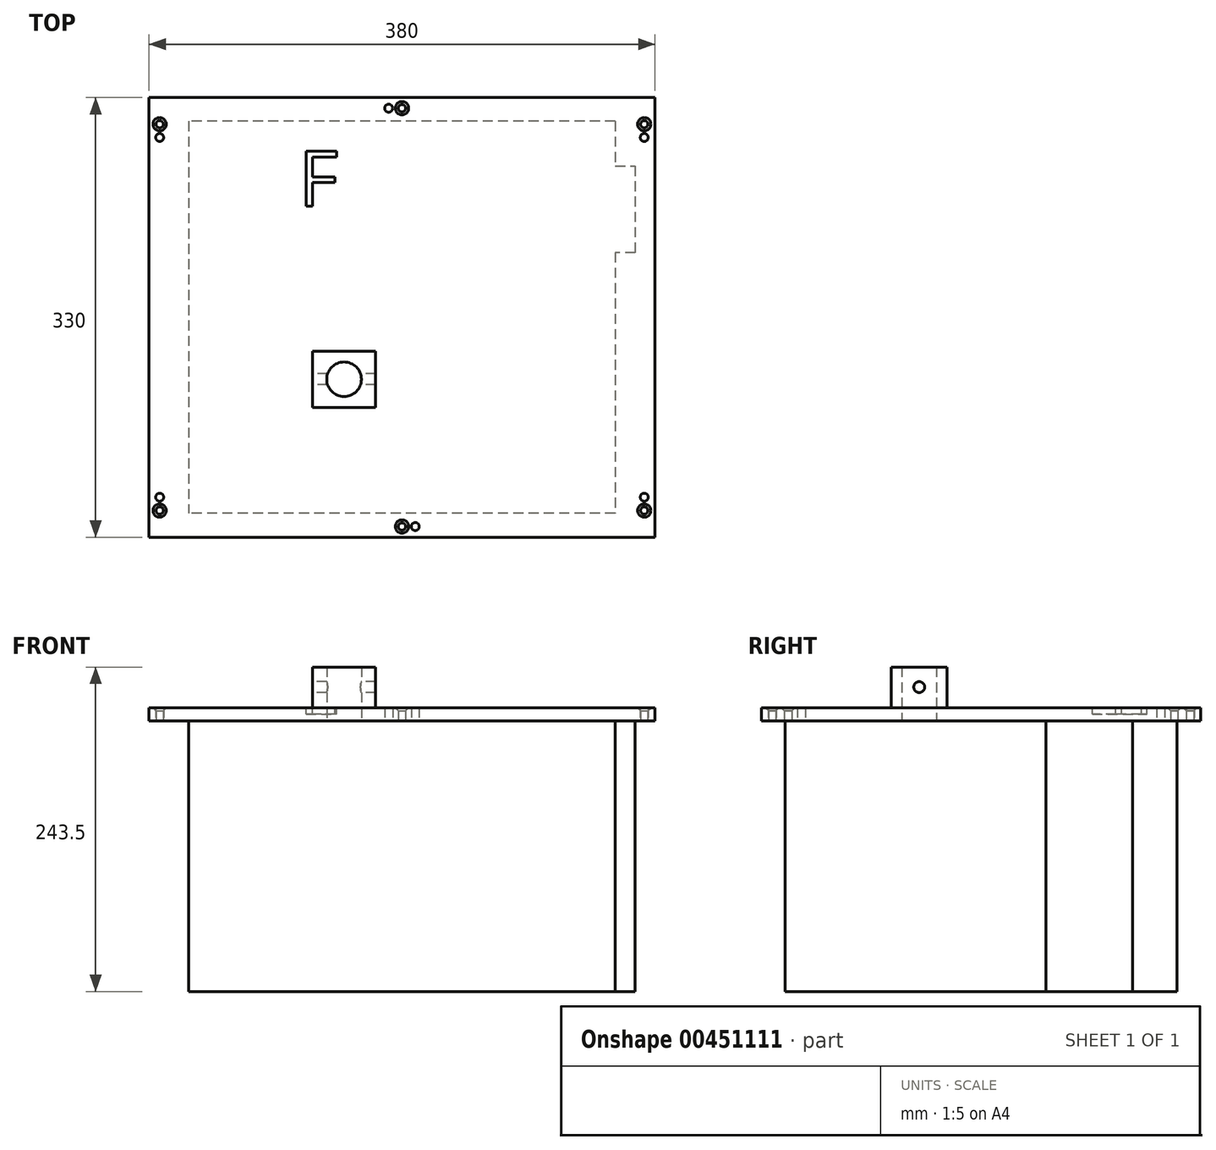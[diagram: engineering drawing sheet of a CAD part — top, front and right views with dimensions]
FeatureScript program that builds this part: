
annotation { "Feature Type Name" : "Feature", "Feature Type Description" : "" }
export const myFeature = defineFeature(function(context is Context, id is Id, definition is map)
    precondition{}
    {
        {
            var Q0;
            Q0=qCreatedBy(makeId("Top.planeOp"),FACE);
            var sketch = newSketch(context, id + "F0", { "sketchPlane" : qUnion([Q0])});
            skLineSegment(sketch, "E0.bottom", {"start": v(190, -165) * mm, "end": v(-190, -165) * mm});
            skLineSegment(sketch, "E0.top", {"start": v(190, 165) * mm, "end": v(-190, 165) * mm});
            skLineSegment(sketch, "E0.left", {"start": v(190, -165) * mm, "end": v(190, 165) * mm});
            skLineSegment(sketch, "E0.right", {"start": v(-190, -165) * mm, "end": v(-190, 165) * mm});
            skPoint(sketch, "E0.middle", {"position": v(0, 0) * mm});
            skSolve(sketch);
        }
        {
            var Q0;
            Q0 = qSketchRegion(id + "F0", true);
            extrude(context, id + "F1", {"entities" : qUnion([Q0]), "depth" : 10 * mm});
        }
        {
            var Q0;
            Q0=makeQuery(id+"F1.opExtrude","CAP_FACE",FACE,{"disambiguationData":[OSD([sQuery(id+"F0.wireOp",EDGE,"E0.bottom"),sQuery(id+"F0.wireOp",EDGE,"E0.top"),sQuery(id+"F0.wireOp",EDGE,"E0.left"),sQuery(id+"F0.wireOp",EDGE,"E0.right")])],"isStart":true});
            var sketch = newSketch(context, id + "F2", { "sketchPlane" : qUnion([Q0])});
            skLineSegment(sketch, "E1.bottom", {"start": v(160.15, -147.15) * mm, "end": v(-160.15, -147.15) * mm});
            skLineSegment(sketch, "E1.top", {"start": v(160.15, 147.15) * mm, "end": v(-160.15, 147.15) * mm});
            skLineSegment(sketch, "E1.left", {"start": v(160.15, -147.15) * mm, "end": v(160.15, 147.15) * mm});
            skLineSegment(sketch, "E1.right", {"start": v(-160.15, -147.15) * mm, "end": v(-160.15, 147.15) * mm});
            skPoint(sketch, "E1.middle", {"position": v(0, 0) * mm});
            skLineSegment(sketch, "E2", {"start": v(160.15, -113.65) * mm, "end": v(175.15, -113.65) * mm});
            skLineSegment(sketch, "E3", {"start": v(175.15, -113.65) * mm, "end": v(175.15, -48.65) * mm});
            skLineSegment(sketch, "E4", {"start": v(175.15, -48.65) * mm, "end": v(160.15, -48.65) * mm});
            skSolve(sketch);
        }
        {
            var Q0;
            Q0 = qSketchRegion(id + "F2", true);
            extrude(context, id + "F3", {"entities" : qUnion([Q0]), "operationType" : NewBodyOperationType.ADD, "depth" : 203 * mm});
        }
        {
            var Q0;
            {var subQ0=sQuery(id+"F0.wireOp",EDGE,"E0.left");var subQ1=sQuery(id+"F0.wireOp",EDGE,"E0.top");var subQ2=sQuery(id+"F0.wireOp",EDGE,"E0.right");var subQ3=sQuery(id+"F0.wireOp",EDGE,"E0.bottom");Q0=makeQuery(id+"F8.boolean.opBoolean","SPLIT",FACE,{"disambiguationData":[TD([makeQuery(id+"F1.opExtrude","SWEPT_FACE",FACE,{"disambiguationData":[OSD([subQ3])]})])],"derivedFrom":makeQuery(id+"F1.opExtrude","CAP_FACE",FACE,{"disambiguationData":[OSD([subQ3,subQ1,subQ0,subQ2])],"isStart":false})});}
            var sketch = newSketch(context, id + "F4", { "sketchPlane" : qUnion([Q0])});
            skPoint(sketch, "E5", {"position": v(0, 157) * mm});
            skPoint(sketch, "E6", {"position": v(0, -157) * mm});
            skPoint(sketch, "E7", {"position": v(-182, 145) * mm});
            skPoint(sketch, "E8", {"position": v(-182, -145) * mm});
            skPoint(sketch, "E9", {"position": v(-182, 135) * mm});
            skPoint(sketch, "E10", {"position": v(-182, -135) * mm});
            skPoint(sketch, "E11.MirrorP", {"position": v(182, 145) * mm});
            skPoint(sketch, "E12.MirrorP", {"position": v(182, -145) * mm});
            skPoint(sketch, "E13.MirrorP", {"position": v(182, 135) * mm});
            skPoint(sketch, "E14.MirrorP", {"position": v(182, -135) * mm});
            skPoint(sketch, "E15", {"position": v(-10, 157) * mm});
            skPoint(sketch, "E16", {"position": v(10, -157) * mm});
            skPoint(sketch, "E17.middle", {"position": v(0, 0) * mm});
            skPoint(sketch, "E18", {"position": v(-43.5, -46.5) * mm});
            skSolve(sketch);
        }
        {
            var Q0;
            Q0=sQuery(id+"F4.wireOp",VERTEX,"E9");
            var Q1;
            Q1=sQuery(id+"F4.wireOp",VERTEX,"E10");
            var Q2;
            Q2=sQuery(id+"F4.wireOp",VERTEX,"E13.MirrorP");
            var Q3;
            Q3=sQuery(id+"F4.wireOp",VERTEX,"E14.MirrorP");
            var Q4;
            Q4=sQuery(id+"F4.wireOp",VERTEX,"E16");
            var Q5;
            Q5=sQuery(id+"F4.wireOp",VERTEX,"E15");
            var Q6;
            Q6=makeQuery(id+"F1.opExtrude","SWEPT_BODY",BODY,{"disambiguationData":[OSD([sQuery(id+"F0.wireOp",EDGE,"E0.bottom"),sQuery(id+"F0.wireOp",EDGE,"E0.top"),sQuery(id+"F0.wireOp",EDGE,"E0.left"),sQuery(id+"F0.wireOp",EDGE,"E0.right")])]});
            hole(context, id + "F5", {"style" : HoleStyle.SIMPLE, "endStyle" : HoleEndStyle.BLIND, "holeDiameter" : 6 * mm, "holeDepth" : 10 * mm, "tappedDepth" : 12 * mm, "tapClearance" : 3, "locations" : qUnion([Q0, Q1, Q2, Q3, Q4, Q5]), "scope" : qUnion([Q6])});
        }
        {
            var Q0;
            Q0=sQuery(id+"F4.wireOp",VERTEX,"E7");
            var Q1;
            Q1=sQuery(id+"F4.wireOp",VERTEX,"E11.MirrorP");
            var Q2;
            Q2=sQuery(id+"F4.wireOp",VERTEX,"E8");
            var Q3;
            Q3=sQuery(id+"F4.wireOp",VERTEX,"E12.MirrorP");
            var Q4;
            Q4=sQuery(id+"F4.wireOp",VERTEX,"E6");
            var Q5;
            Q5=sQuery(id+"F4.wireOp",VERTEX,"E5");
            var Q6;
            Q6=makeQuery(id+"F1.opExtrude","SWEPT_BODY",BODY,{"disambiguationData":[OSD([sQuery(id+"F0.wireOp",EDGE,"E0.bottom"),sQuery(id+"F0.wireOp",EDGE,"E0.top"),sQuery(id+"F0.wireOp",EDGE,"E0.left"),sQuery(id+"F0.wireOp",EDGE,"E0.right")])]});
            hole(context, id + "F6", {"style" : HoleStyle.C_SINK, "endStyle" : HoleEndStyle.BLIND, "holeDiameter" : 5.5 * mm, "cSinkDiameter" : 10 * mm, "cSinkAngle" : 90 * degree, "holeDepth" : 10 * mm, "tappedDepth" : 12 * mm, "tapClearance" : 3, "locations" : qUnion([Q0, Q1, Q2, Q3, Q4, Q5]), "scope" : qUnion([Q6])});
        }
        {
            var Q0;
            Q0=makeQuery(id+"F1.opExtrude","CAP_FACE",FACE,{"disambiguationData":[OSD([sQuery(id+"F0.wireOp",EDGE,"E0.bottom"),sQuery(id+"F0.wireOp",EDGE,"E0.top"),sQuery(id+"F0.wireOp",EDGE,"E0.left"),sQuery(id+"F0.wireOp",EDGE,"E0.right")])],"isStart":false});
            var sketch = newSketch(context, id + "F7", { "sketchPlane" : qUnion([Q0])});
            skLineSegment(sketch, "E19.bottom", {"start": v(-19.75, -67.5) * mm, "end": v(-67.25, -67.5) * mm});
            skLineSegment(sketch, "E19.top", {"start": v(-19.75, -25.5) * mm, "end": v(-67.25, -25.5) * mm});
            skLineSegment(sketch, "E19.left", {"start": v(-19.75, -67.5) * mm, "end": v(-19.75, -25.5) * mm});
            skLineSegment(sketch, "E19.right", {"start": v(-67.25, -67.5) * mm, "end": v(-67.25, -25.5) * mm});
            skPoint(sketch, "E19.middle", {"position": v(-43.5, -46.5) * mm});
            skCircle(sketch, "E20", {"center": v(-43.5, -46.5) * mm, "radius": 13 * mm});
            skSolve(sketch);
        }
        {
            var Q0;
            Q0 = qSketchRegion(id + "F7", true);
            extrude(context, id + "F8", {"entities" : qUnion([Q0]), "operationType" : NewBodyOperationType.ADD, "depth" : 30.5 * mm});
        }
        {
            var Q0;
            {var subQ0=sQuery(id+"F0.wireOp",EDGE,"E0.left");var subQ1=sQuery(id+"F0.wireOp",EDGE,"E0.top");var subQ2=sQuery(id+"F0.wireOp",EDGE,"E0.right");var subQ3=sQuery(id+"F0.wireOp",EDGE,"E0.bottom");Q0=makeQuery(id+"F8.boolean.opBoolean","SPLIT",FACE,{"disambiguationData":[TD([makeQuery(id+"F1.opExtrude","SWEPT_FACE",FACE,{"disambiguationData":[OSD([subQ3])]})])],"derivedFrom":makeQuery(id+"F1.opExtrude","CAP_FACE",FACE,{"disambiguationData":[OSD([subQ3,subQ1,subQ0,subQ2])],"isStart":false})});}
            var sketch = newSketch(context, id + "F9", { "sketchPlane" : qUnion([Q0])});
            skText(sketch, "E21", { "text": "F", "fontName": "OpenSans-Regular.ttf"});
            const initialGuessF9  = {"E21": [-0.07771, 0.0835, 1, 0, 0.04155]};
            skSetInitialGuess(sketch, initialGuessF9);
            skSolve(sketch);
        }
        {
            var Q0;
            Q0 = qSketchRegion(id + "F9", true);
            extrude(context, id + "F10", {"entities" : qUnion([Q0]), "operationType" : NewBodyOperationType.REMOVE, "oppositeDirection" : true, "depth" : 5 * mm, "offsetDistance" : 25 * mm});
        }
        {
            var Q0;
            Q0=makeQuery(id+"F8.opExtrude","SWEPT_FACE",FACE,{"disambiguationData":[OSD([sQuery(id+"F7.wireOp",EDGE,"E19.right")])]});
            var sketch = newSketch(context, id + "F11", { "sketchPlane" : qUnion([Q0])});
            skCircle(sketch, "E22", {"center": v(46.5, 25.5) * mm, "radius": 4.1 * mm});
            skSolve(sketch);
        }
        {
            var Q0;
            Q0 = qSketchRegion(id + "F11", true);
            extrude(context, id + "F12", {"entities" : qUnion([Q0]), "operationType" : NewBodyOperationType.REMOVE, "oppositeDirection" : true, "depth" : 62.5 * mm, "offsetDistance" : 25 * mm});
        }
        {
            var Q0;
            Q0=makeQuery(id+"F8.boolean.opBoolean","SPLIT",FACE,{"disambiguationData":[TD([makeQuery(id+"F8.opExtrude","SWEPT_FACE",FACE,{"disambiguationData":[OSD([sQuery(id+"F7.wireOp",EDGE,"E20")])]})])],"derivedFrom":makeQuery(id+"F1.opExtrude","CAP_FACE",FACE,{"disambiguationData":[OSD([sQuery(id+"F0.wireOp",EDGE,"E0.bottom"),sQuery(id+"F0.wireOp",EDGE,"E0.top"),sQuery(id+"F0.wireOp",EDGE,"E0.left"),sQuery(id+"F0.wireOp",EDGE,"E0.right")])],"isStart":false})});
            extrude(context, id + "F13", {"entities" : qUnion([Q0]), "operationType" : NewBodyOperationType.REMOVE, "oppositeDirection" : true, "depth" : 10 * mm, "offsetDistance" : 25 * mm});
        }
    });
